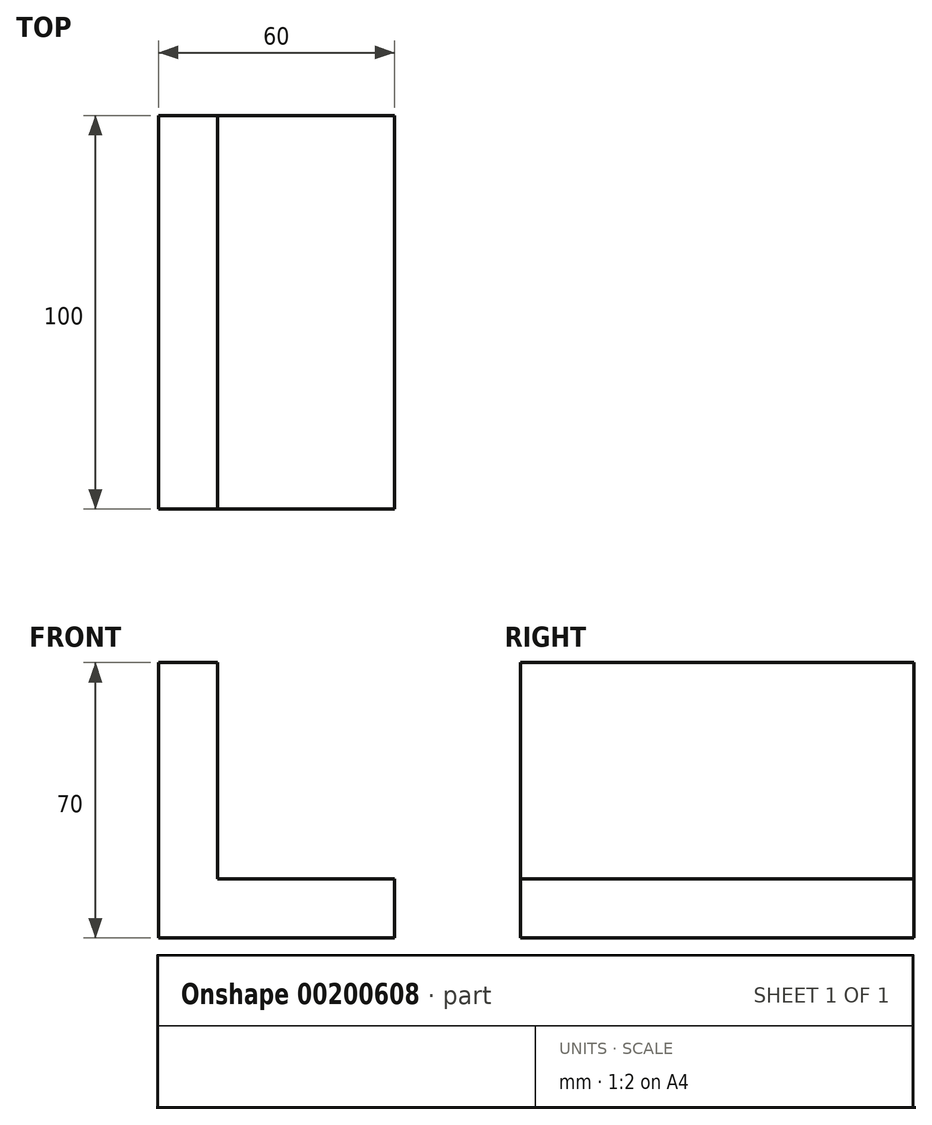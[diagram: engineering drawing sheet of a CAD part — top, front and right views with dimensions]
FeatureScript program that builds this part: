
annotation { "Feature Type Name" : "Feature", "Feature Type Description" : "" }
export const myFeature = defineFeature(function(context is Context, id is Id, definition is map)
    precondition{}
    {
        {
            var Q0;
            Q0=qCreatedBy(makeId("Front.planeOp"),FACE);
            var sketch = newSketch(context, id + "F0", { "sketchPlane" : qUnion([Q0])});
            skLineSegment(sketch, "E0.bottom", {"start": v(-60, 70) * mm, "end": v(-45, 70) * mm});
            skLineSegment(sketch, "E0.top", {"start": v(-60, 0) * mm, "end": v(-45, 0) * mm});
            skLineSegment(sketch, "E0.left", {"start": v(-60, 70) * mm, "end": v(-60, 0) * mm});
            skLineSegment(sketch, "E0.right", {"start": v(-45, 70) * mm, "end": v(-45, 0) * mm});
            skLineSegment(sketch, "E1.bottom", {"start": v(-45, 15) * mm, "end": v(0, 15) * mm});
            skLineSegment(sketch, "E1.top", {"start": v(-45, 0) * mm, "end": v(0, 0) * mm});
            skLineSegment(sketch, "E1.left", {"start": v(-45, 15) * mm, "end": v(-45, 0) * mm});
            skLineSegment(sketch, "E1.right", {"start": v(0, 15) * mm, "end": v(0, 0) * mm});
            skSolve(sketch);
        }
        {
            var Q0;
            Q0 = qSketchRegion(id + "F0", true);
            extrude(context, id + "F1", {"entities" : qUnion([Q0]), "depth" : 100 * mm});
        }
    });
